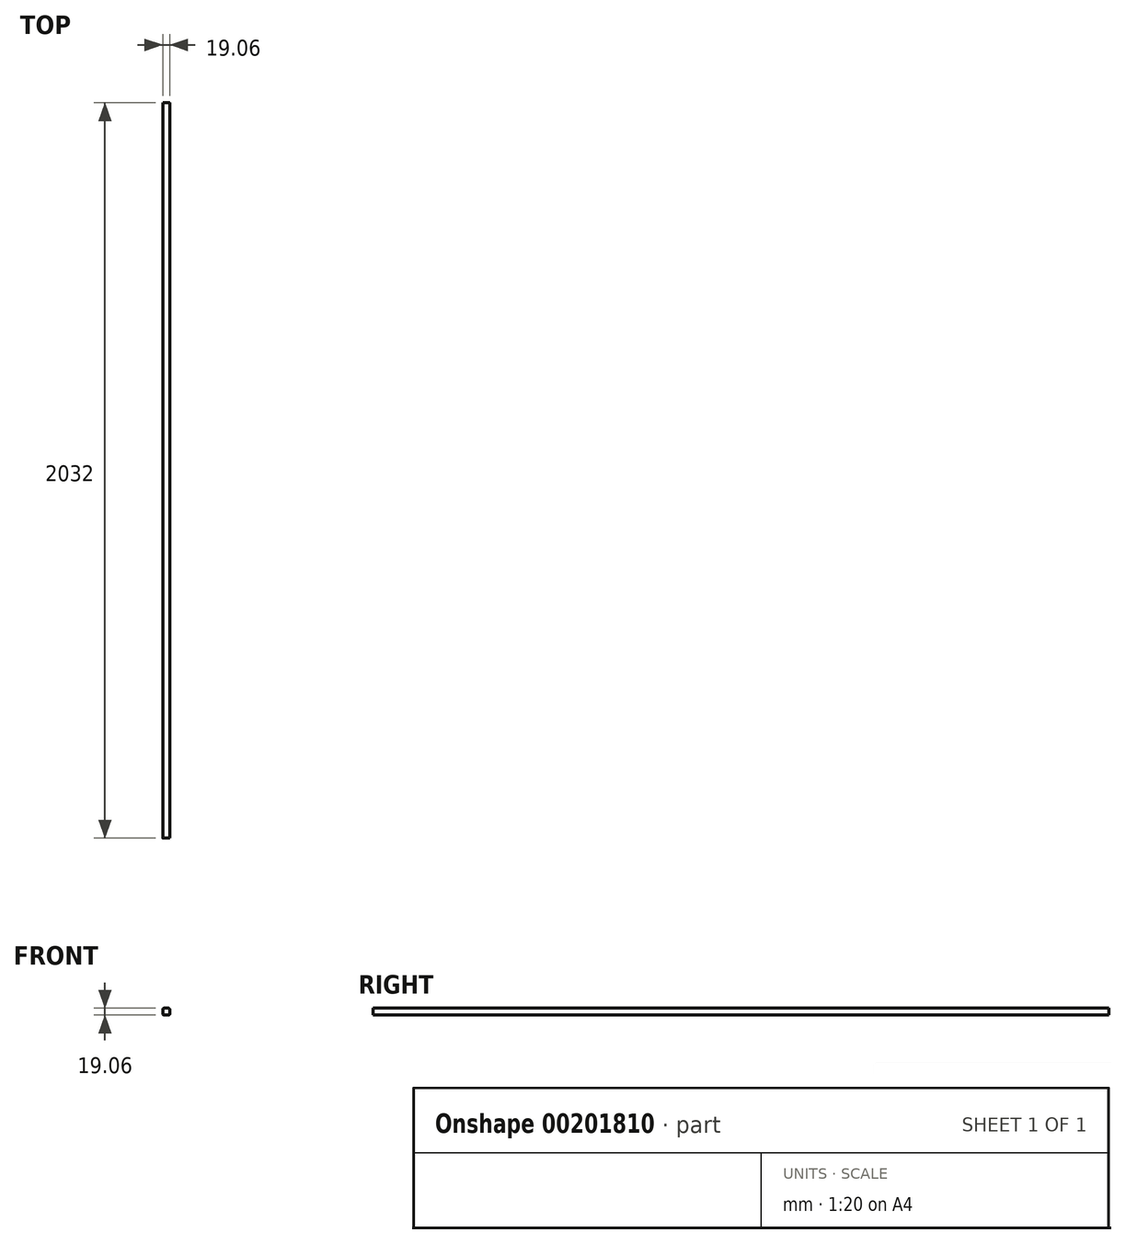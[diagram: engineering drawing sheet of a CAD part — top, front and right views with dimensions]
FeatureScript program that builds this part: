
annotation { "Feature Type Name" : "Feature", "Feature Type Description" : "" }
export const myFeature = defineFeature(function(context is Context, id is Id, definition is map)
    precondition{}
    {
        {
            var Q0;
            Q0=qCreatedBy(makeId("Front.planeOp"),FACE);
            var sketch = newSketch(context, id + "F0", { "sketchPlane" : qUnion([Q0])});
            skLineSegment(sketch, "E0.bottom", {"start": v(6.35, -9.53) * mm, "end": v(-6.35, -9.53) * mm});
            skLineSegment(sketch, "E0.top", {"start": v(6.35, 9.53) * mm, "end": v(-6.35, 9.53) * mm});
            skLineSegment(sketch, "E0.left", {"start": v(9.52, -6.35) * mm, "end": v(9.52, 6.35) * mm});
            skLineSegment(sketch, "E0.right", {"start": v(-9.53, -6.35) * mm, "end": v(-9.53, 6.35) * mm});
            skPoint(sketch, "E0.middle", {"position": v(0, 0) * mm});
            skPoint(sketch, "E1.visualSharp", {"position": v(9.52, 9.53) * mm});
            skArc(sketch, "E1.filletArc", {"start": v(9.52, 6.35) * mm, "mid": v(8.6, 8.6) * mm, "end": v(6.35, 9.53) * mm});
            skPoint(sketch, "E2.visualSharp", {"position": v(9.52, -9.53) * mm});
            skArc(sketch, "E2.filletArc", {"start": v(6.35, -9.53) * mm, "mid": v(8.6, -8.6) * mm, "end": v(9.52, -6.35) * mm});
            skPoint(sketch, "E3.visualSharp", {"position": v(-9.53, 9.52) * mm});
            skArc(sketch, "E3.filletArc", {"start": v(-6.35, 9.53) * mm, "mid": v(-8.6, 8.6) * mm, "end": v(-9.53, 6.35) * mm});
            skPoint(sketch, "E4.visualSharp", {"position": v(-9.53, -9.53) * mm});
            skArc(sketch, "E4.filletArc", {"start": v(-9.53, -6.35) * mm, "mid": v(-8.6, -8.6) * mm, "end": v(-6.35, -9.53) * mm});
            skSolve(sketch);
        }
        {
            var Q0;
            Q0=makeQuery(id+"F0.imprint","IMPRINT",FACE,{"disambiguationData":[TD([[makeQuery(id+"F0.imprint","IMPRINT",EDGE,{"derivedFrom":sQuery(id+"F0.wireOp",EDGE,"E0.bottom")}),-1.0]])]});
            extrude(context, id + "F1", {"entities" : qUnion([Q0]), "depth" : 2032 * mm});
        }
    });
